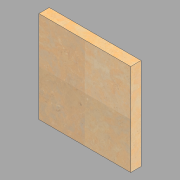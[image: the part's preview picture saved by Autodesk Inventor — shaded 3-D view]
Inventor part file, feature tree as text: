
AUTODESK INVENTOR PART (.ipt)
format: ipt  version: 2022.1 (Build 261234020, 234B)  size: 105,984 bytes
history: native  units: in
note: dims shown in document units (in); Inventor stores cm internally (conversion verified against a paired STEP export)
features: extrude x1, sketch x1
ambient origin geometry x8: Origin, YZ Plane, XZ Plane, XY Plane, X Axis, Y Axis, Z Axis, Center Point
bodies: Solid1 (feature_tree)
feature tree (2):
  extrude  "Extrusion1"  Depth=17.625in
  sketch  "Sketch1"  dims[d0=17.625in d1=17.625in d2=2.0in d3=0.0in]
